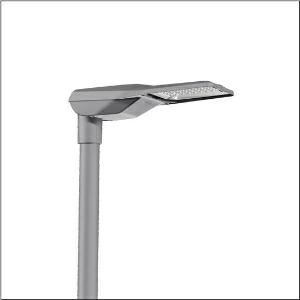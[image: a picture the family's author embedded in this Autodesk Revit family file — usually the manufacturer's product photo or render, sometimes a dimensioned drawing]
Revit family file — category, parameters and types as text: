
# Revit family: streetlight_sl_21_iq_mini___stw1_0a_5xe2e41g08jb_4c9f
name_source: partatom
category: Lighting Fixtures
units: mm (PartAtom-declared; Revit-internal decimal feet)

## family parameters
Cut with Voids When Loaded = No
Host = Face
Light Source = No
Part Type = Normal
Room Calculation Point = No
Round Connector Dimension = Use Diameter
Shared = No

## types (1)
- --- (1 x LED, 11290 lm, 71.6 W, 4000K)
    Apparent Load = 72 VA
    CIE Flux Codes = 39 75 98 100 100
    Color Rendering = 70
    Color Temperature = 4000K
    Default Elevation = 1800 mm
    Description = Streetlight SL 21 iQ mini, mast luminaire, primary light control with lens, of PMMA, primary optical cover: cover, of toughened safety glass, transparent, light distribution: STW1.0a, light emission: direct distribution, primary light characteristic: asymmetric, installation type: post-top, side-entry, LED, High Power LED, rated luminous flux: 11.290lm, luminous efficacy: 158lm/W, light colour: 740, colour temperature: 4000K, control: Street-Remote, Auto-Match, Temp-Guard, Lumen-Switch, Night-Set, Smart-Wire, Light-Fading, Desk-Remote (wireless, voltage-free reading and setting of iQ features in the workshop via application-optimized NFC function/RFID function), optimised constant luminous flux control (CLO 2.0), pre-setting: linear dimming characteristic, mains connection: 220..240V, AC, 50/60Hz, start of lifetime: 72W, end of service life: 75W, reduction: 33W, luminaire housing, of diecast aluminium, powder-coated, Siteco® metallic grey (DB 702S), corrosivity category C5 mid according to DIN EN ISO 12944, please order mast flange separately, inclination adjustable: 0°, 5°, 10°, 15°, sealing non-destructively replaceable, multi-level sealing system, length: 628mm, width: 235mm, height: 110mm, mast flange for spigot size: 42mm (side-entry): 5XC10008XM4, 60/48mm (side-entry/post-top): 5XC10108XM2, 76/60mm (side-entry/post-top): 5XC10108XM1, protection rating (complete): IP66, insulation class (complete): insulation class II (safety insulation), certification: CE, ENEC, ENEC+, VDE, impact resistance: IK09, permissible operating ambient temperature for outdoor applications: -40..+50°C, standard-compliant lighting for roads and squares, packaging unit: 1 piece

Light Distribution: STW1.0a
    Height = 110 mm
    Lamp = 1 x LED
    Lamp Light Flux = 11290 lm
    Lamp Power = 71.6 W
    Lamp count = 1
    Length = 625 mm
    Luminous efficacy = 158 lm/W
    Manufacturer = Siteco
    ModVariant = No
    Model = 5XE2E41G08JB
    Number of Poles = 1
    OnlyDefault = Yes
    Power Factor = 1
    Product Name = Streetlight SL 21 iQ mini | STW1.0a
    Product group = mast luminaire | pylon top
    ProductGroupID = 6100
    Protection Class = Protection class II
    Protection Degree = IP 66
    RLX_Detail_Level = 1
    RLX_Emergency_Light_Flux = 0 lm
    RLX_Emergency_Type = 0
    RLX_Emergency_Type_DB = No
    RlxData = <blob elided: 92333 chars, md5=c2805a59>
    Socket = socket
    Standby Power = 0 W
    System Light Flux = 11290 lm
    System Power = 72 W
    Type Comments = factory setting: luminous flux: 100 % | dim-lin: 254 | 746 mA
    Type Image = l_1003519.jpg
    URL = http://relux.com
    VarID = @adj_140887
    Voltage = 0 V
    Weight = 0.00 kg
    Width = 234 mm

## geometry (parser evidence)
native form markers: Blend x4, Sweep x11
no freeform markers — native parametric forms only
